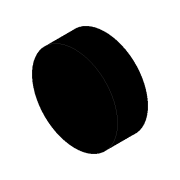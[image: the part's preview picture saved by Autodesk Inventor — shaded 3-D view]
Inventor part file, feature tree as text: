
AUTODESK INVENTOR PART (.ipt)
format: ipt  version: 2020 (Build 240168000, 168)  size: 85,504 bytes
history: native  units: mm
features: other x1, extrude x1, sketch x1
ambient origin geometry x8: Origin, YZ Plane, XZ Plane, XY Plane, X Axis, Y Axis, Z Axis, Center Point
bodies: Body1 (feature_tree)
feature tree (3):
  other  "솔리드1"
  extrude  "돌출1"  Depth=42.4mm
  sketch  "스케치1"
